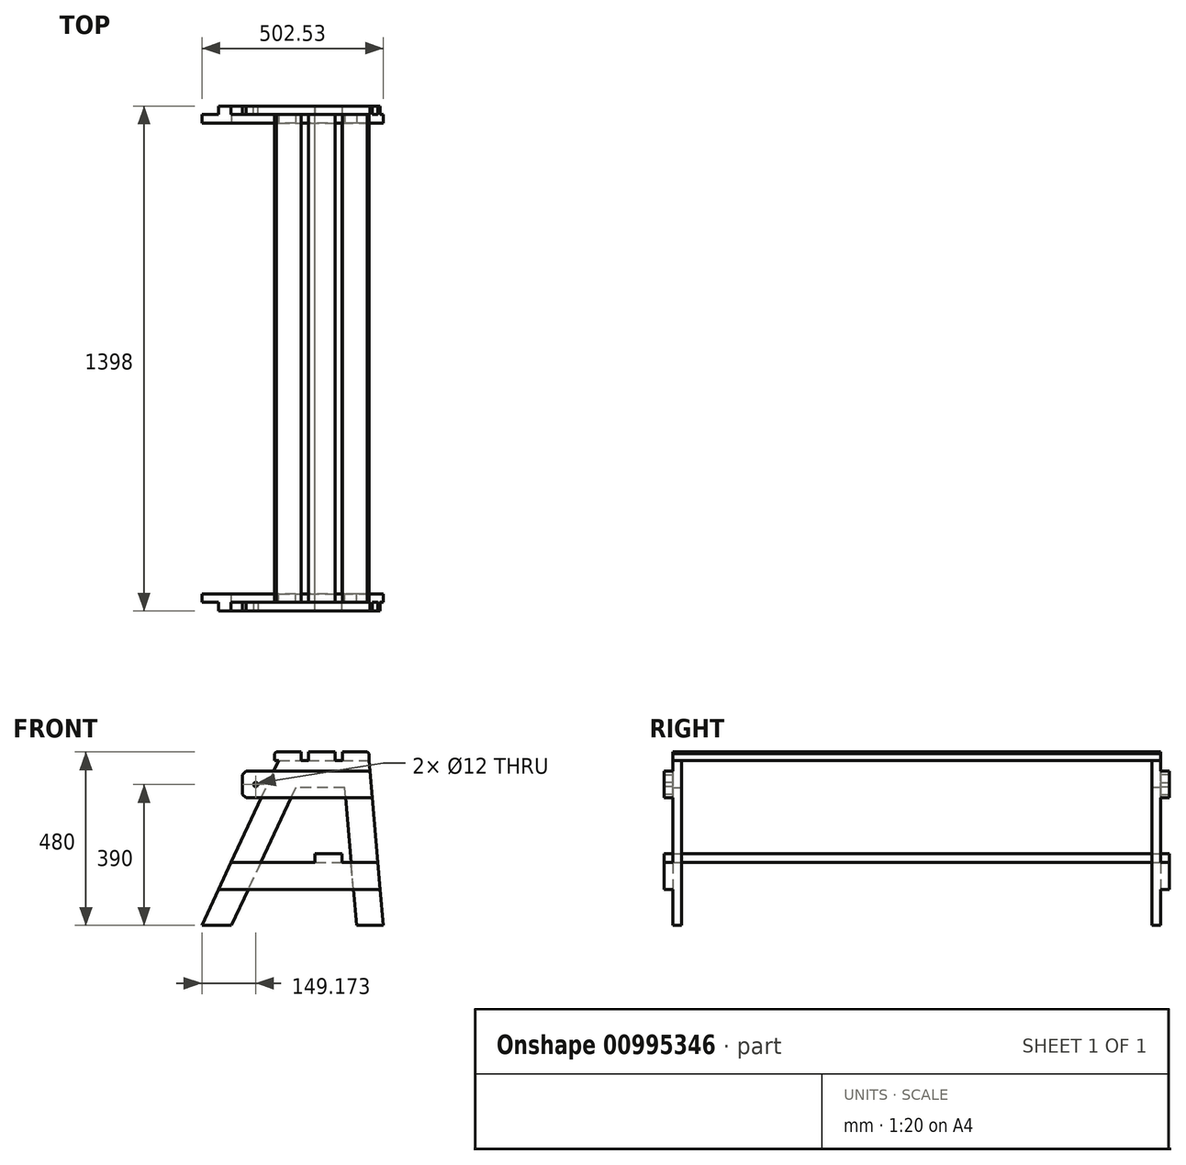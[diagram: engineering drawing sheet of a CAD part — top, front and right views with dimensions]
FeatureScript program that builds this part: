
annotation { "Feature Type Name" : "Feature", "Feature Type Description" : "" }
export const myFeature = defineFeature(function(context is Context, id is Id, definition is map)
    precondition{}
    {
        {
            assignVariable(context, id + "F0", {"name" : "Lattendicke", "anyValue" : 24});
        }
        {
            var Q0;
            Q0=qCreatedBy(makeId("Front.planeOp"),FACE);
            var sketch = newSketch(context, id + "F1", { "sketchPlane" : qUnion([Q0])});
            skLineSegment(sketch, "E0", {"start": v(0, 0) * mm, "end": v(212.64, 456) * mm});
            skLineSegment(sketch, "E1", {"start": v(212.64, 456) * mm, "end": v(462.64, 456) * mm});
            skLineSegment(sketch, "E2", {"start": v(462.64, 456) * mm, "end": v(502.53, 0) * mm});
            skLineSegment(sketch, "E3", {"start": v(502.53, 0) * mm, "end": v(428.25, 0) * mm});
            skLineSegment(sketch, "E4", {"start": v(428.25, 0) * mm, "end": v(394.83, 382) * mm});
            skLineSegment(sketch, "E5", {"start": v(394.83, 382) * mm, "end": v(259.78, 382) * mm});
            skLineSegment(sketch, "E6", {"start": v(259.78, 382) * mm, "end": v(81.65, 0) * mm});
            skLineSegment(sketch, "E7", {"start": v(81.65, 0) * mm, "end": v(0, 0) * mm});
            skSolve(sketch);
        }
        {
            var Q0;
            Q0 = qSketchRegion(id + "F1", true);
            extrude(context, id + "F2", {"entities" : qUnion([Q0]), "depth" : (getVariable(context, 'Lattendicke')) * mm, "offsetDistance" : 25 * mm});
        }
        {
            var Q0;
            Q0=makeQuery(id+"F2.opExtrude","CAP_FACE",FACE,{"disambiguationData":[OSD([sQuery(id+"F1.wireOp",EDGE,"E0"),sQuery(id+"F1.wireOp",EDGE,"E1"),sQuery(id+"F1.wireOp",EDGE,"E2"),sQuery(id+"F1.wireOp",EDGE,"E3"),sQuery(id+"F1.wireOp",EDGE,"E4"),sQuery(id+"F1.wireOp",EDGE,"E5"),sQuery(id+"F1.wireOp",EDGE,"E6"),sQuery(id+"F1.wireOp",EDGE,"E7")])],"isStart":false});
            var sketch = newSketch(context, id + "F3", { "sketchPlane" : qUnion([Q0])});
            skLineSegment(sketch, "E8", {"start": v(465.17, 427) * mm, "end": v(112.17, 427) * mm});
            skLineSegment(sketch, "E9", {"start": v(112.17, 427) * mm, "end": v(112.17, 353) * mm});
            skLineSegment(sketch, "E10", {"start": v(112.17, 353) * mm, "end": v(471.65, 353) * mm});
            skLineSegment(sketch, "E11", {"start": v(471.65, 353) * mm, "end": v(465.17, 427) * mm});
            skLineSegment(sketch, "E12", {"start": v(81.14, 174) * mm, "end": v(487.3, 174) * mm});
            skLineSegment(sketch, "E13", {"start": v(487.3, 174) * mm, "end": v(493.78, 100) * mm});
            skLineSegment(sketch, "E14", {"start": v(493.78, 100) * mm, "end": v(46.63, 100) * mm});
            skLineSegment(sketch, "E15", {"start": v(46.63, 100) * mm, "end": v(81.14, 174) * mm});
            skSolve(sketch);
        }
        {
            var Q0;
            {var subQ3=sQuery(id+"F3.wireOp",EDGE,"E9");Q0=makeQuery(id+"F3.imprint","IMPRINT",FACE,{"disambiguationData":[TD([[makeQuery(id+"F3.imprint","IMPRINT",EDGE,{"derivedFrom":subQ3}),1.0]])]});}
            var Q1;
            {var subQ2=sQuery(id+"F3.wireOp",EDGE,"E11");Q1=makeQuery(id+"F3.imprint","IMPRINT",FACE,{"disambiguationData":[TD([[makeQuery(id+"F3.imprint","IMPRINT",EDGE,{"derivedFrom":subQ2}),-1.0]])]});}
            var Q2;
            {var subQ0=sQuery(id+"F3.wireOp",EDGE,"E12");var subQ1=makeQuery(id+"F2.opExtrude","CAP_EDGE",EDGE,{"disambiguationData":[OSD([sQuery(id+"F1.wireOp",EDGE,"E6")])],"isStart":false});var subQ2=makeQuery(id+"F3.imprint","INTERSECT",VERTEX,{"derivedFrom":[subQ1,subQ0]});Q2=makeQuery(id+"F3.imprint","IMPRINT",FACE,{"disambiguationData":[TD([[makeQuery(id+"F3.imprint","IMPRINT",EDGE,{"disambiguationData":[TD([[subQ2,-1.0]])],"derivedFrom":subQ0}),-1.0]])]});}
            var Q3;
            {var subQ0=sQuery(id+"F3.wireOp",EDGE,"E15");Q3=makeQuery(id+"F3.imprint","IMPRINT",FACE,{"disambiguationData":[TD([[makeQuery(id+"F3.imprint","IMPRINT",EDGE,{"derivedFrom":subQ0}),-1.0]])]});}
            var Q4;
            {var subQ0=sQuery(id+"F3.wireOp",EDGE,"E13");Q4=makeQuery(id+"F3.imprint","IMPRINT",FACE,{"disambiguationData":[TD([[makeQuery(id+"F3.imprint","IMPRINT",EDGE,{"derivedFrom":subQ0}),-1.0]])]});}
            var Q5;
            {var subQ5=makeQuery(id+"F2.opExtrude","CAP_EDGE",EDGE,{"disambiguationData":[OSD([sQuery(id+"F1.wireOp",EDGE,"E5")])],"isStart":false});Q5=makeQuery(id+"F3.imprint","IMPRINT",FACE,{"disambiguationData":[TD([[makeQuery(id+"F3.imprint","IMPRINT",EDGE,{"derivedFrom":subQ5}),1.0]])]});}
            extrude(context, id + "F4", {"entities" : qUnion([Q0, Q1, Q2, Q3, Q4, Q5]), "operationType" : NewBodyOperationType.ADD, "depth" : (getVariable(context, 'Lattendicke')) * mm, "offsetDistance" : 25 * mm});
        }
        {
            var Q0;
            Q0=makeQuery(id+"F4.opExtrude","SWEPT_FACE",FACE,{"disambiguationData":[OSD([sQuery(id+"F3.wireOp",EDGE,"E12")])]});
            var sketch = newSketch(context, id + "F5", { "sketchPlane" : qUnion([Q0])});
            skLineSegment(sketch, "E16.bottom", {"start": v(313.3, -48) * mm, "end": v(387.3, -48) * mm});
            skLineSegment(sketch, "E16.top", {"start": v(313.3, 651) * mm, "end": v(387.3, 651) * mm});
            skLineSegment(sketch, "E16.left", {"start": v(313.3, -48) * mm, "end": v(313.3, 651) * mm});
            skLineSegment(sketch, "E16.right", {"start": v(387.3, -48) * mm, "end": v(387.3, 651) * mm});
            skLineSegment(sketch, "E17", {"start": v(350.3, -48) * mm, "end": v(350.3, 651) * mm, "construction": true});
            skSolve(sketch);
        }
        {
            var Q0;
            Q0 = qSketchRegion(id + "F5", true);
            extrude(context, id + "F6", {"entities" : qUnion([Q0]), "operationType" : NewBodyOperationType.ADD, "depth" : (getVariable(context, 'Lattendicke')) * mm, "offsetDistance" : 25 * mm});
        }
        {
            var Q0;
            Q0=makeQuery(id+"FZW4tMHVHPS0k4L_1.boolean.opBoolean","MERGE",FACE,{"derivedFrom":[makeQuery(id+"F4.opExtrude","CAP_FACE",FACE,{"disambiguationData":[OSD([sQuery(id+"F3.wireOp",EDGE,"E8"),sQuery(id+"F3.wireOp",EDGE,"E9"),sQuery(id+"F3.wireOp",EDGE,"E10"),sQuery(id+"F3.wireOp",EDGE,"E11")])],"isStart":false}),makeQuery(id+"FZW4tMHVHPS0k4L_1.opExtrude","SWEPT_FACE",FACE,{"disambiguationData":[OSD([sQuery(id+"FmopSP1TCN60EbX_1.wireOp",EDGE,"fZKEBfGV-dzuW-k69T-f120-0Okk8d1ObTub.bottom")])]}),makeQuery(id+"FZW4tMHVHPS0k4L_1.opExtrude","SWEPT_FACE",FACE,{"disambiguationData":[OSD([sQuery(id+"FmopSP1TCN60EbX_1.wireOp",EDGE,"MPfSMtai-v8oZ-TTrc-7ozS-PhWWdRkUMMTi.bottom")])]}),makeQuery(id+"FZW4tMHVHPS0k4L_1.opExtrude","SWEPT_FACE",FACE,{"disambiguationData":[OSD([sQuery(id+"FmopSP1TCN60EbX_1.wireOp",EDGE,"9iwYwjk1-Ofcv-kupA-KBHU-Erxazx1jPGkJ.bottom")])]})]});
            var sketch = newSketch(context, id + "F7", { "sketchPlane" : qUnion([Q0])});
            skCircle(sketch, "E18", {"center": v(149.17, 390) * mm, "radius": 6 * mm});
            skSolve(sketch);
        }
        {
            var Q0;
            Q0=makeQuery(id+"F7.imprint","IMPRINT",FACE,{"disambiguationData":[TD([[makeQuery(id+"F7.imprint","IMPRINT",EDGE,{"derivedFrom":sQuery(id+"F7.wireOp",EDGE,"E18")}),1.0]])]});
            extrude(context, id + "F8", {"entities" : qUnion([Q0]), "operationType" : NewBodyOperationType.REMOVE, "endBound" : BoundingType.THROUGH_ALL, "oppositeDirection" : true, "depth" : 25 * mm, "offsetDistance" : 25 * mm});
        }
        {
            var Q0;
            Q0=makeQuery(id+"F4.opExtrude","SWEPT_EDGE",EDGE,{"disambiguationData":[OSD([sQuery(id+"F3.wireOp",EDGE,"E8"),sQuery(id+"F3.wireOp",EDGE,"E9")])]});
            var Q1;
            Q1=makeQuery(id+"F4.opExtrude","SWEPT_EDGE",EDGE,{"disambiguationData":[OSD([sQuery(id+"F3.wireOp",EDGE,"E9"),sQuery(id+"F3.wireOp",EDGE,"E10")])]});
            chamfer(context, id + "F9", {"entities" : qUnion([Q0, Q1]), "width" : 10 * mm, "tangentPropagation" : true});
        }
        {
            var Q0;
            Q0=makeQuery(id+"F2.opExtrude","SWEPT_FACE",FACE,{"disambiguationData":[OSD([sQuery(id+"F1.wireOp",EDGE,"E1")])]});
            var sketch = newSketch(context, id + "F10", { "sketchPlane" : qUnion([Q0])});
            skLineSegment(sketch, "E19.bottom", {"start": v(462.64, -24) * mm, "end": v(388.64, -24) * mm});
            skLineSegment(sketch, "E19.top", {"start": v(462.64, 651) * mm, "end": v(388.64, 651) * mm});
            skLineSegment(sketch, "E19.left", {"start": v(462.64, -24) * mm, "end": v(462.64, 651) * mm});
            skLineSegment(sketch, "E19.right", {"start": v(388.64, -24) * mm, "end": v(388.64, 651) * mm});
            skLineSegment(sketch, "E20.bottom", {"start": v(368.64, -24) * mm, "end": v(294.64, -24) * mm});
            skLineSegment(sketch, "E20.top", {"start": v(368.64, 651) * mm, "end": v(294.64, 651) * mm});
            skLineSegment(sketch, "E20.left", {"start": v(368.64, -24) * mm, "end": v(368.64, 651) * mm});
            skLineSegment(sketch, "E20.right", {"start": v(294.64, -24) * mm, "end": v(294.64, 651) * mm});
            skLineSegment(sketch, "E21.bottom", {"start": v(274.64, -24) * mm, "end": v(200.64, -24) * mm});
            skLineSegment(sketch, "E21.top", {"start": v(274.64, 651) * mm, "end": v(200.64, 651) * mm});
            skLineSegment(sketch, "E21.left", {"start": v(274.64, -24) * mm, "end": v(274.64, 651) * mm});
            skLineSegment(sketch, "E21.right", {"start": v(200.64, -24) * mm, "end": v(200.64, 651) * mm});
            skSolve(sketch);
        }
        {
            var Q0;
            {var subQ0=sQuery(id+"F10.wireOp",EDGE,"E19.top");Q0=makeQuery(id+"F10.imprint","IMPRINT",FACE,{"disambiguationData":[TD([[makeQuery(id+"F10.imprint","IMPRINT",EDGE,{"derivedFrom":subQ0}),1.0]])]});}
            var Q1;
            {var subQ0=sQuery(id+"F10.wireOp",EDGE,"E20.top");Q1=makeQuery(id+"F10.imprint","IMPRINT",FACE,{"disambiguationData":[TD([[makeQuery(id+"F10.imprint","IMPRINT",EDGE,{"derivedFrom":subQ0}),1.0]])]});}
            var Q2;
            {var subQ0=sQuery(id+"F10.wireOp",EDGE,"E19.bottom");Q2=makeQuery(id+"F10.imprint","IMPRINT",FACE,{"disambiguationData":[TD([[makeQuery(id+"F10.imprint","IMPRINT",EDGE,{"derivedFrom":subQ0}),1.0]])]});}
            var Q3;
            {var subQ0=sQuery(id+"F10.wireOp",EDGE,"E20.bottom");Q3=makeQuery(id+"F10.imprint","IMPRINT",FACE,{"disambiguationData":[TD([[makeQuery(id+"F10.imprint","IMPRINT",EDGE,{"derivedFrom":subQ0}),1.0]])]});}
            var Q4;
            {var subQ0=sQuery(id+"F10.wireOp",EDGE,"E21.bottom");Q4=makeQuery(id+"F10.imprint","IMPRINT",FACE,{"disambiguationData":[TD([[makeQuery(id+"F10.imprint","IMPRINT",EDGE,{"derivedFrom":subQ0}),1.0]])]});}
            var Q5;
            {var subQ0=sQuery(id+"F10.wireOp",EDGE,"E21.top");Q5=makeQuery(id+"F10.imprint","IMPRINT",FACE,{"disambiguationData":[TD([[makeQuery(id+"F10.imprint","IMPRINT",EDGE,{"derivedFrom":subQ0}),1.0]])]});}
            extrude(context, id + "F11", {"entities" : qUnion([Q0, Q1, Q2, Q3, Q4, Q5]), "operationType" : NewBodyOperationType.ADD, "depth" : (getVariable(context, 'Lattendicke')) * mm, "offsetDistance" : 25 * mm});
        }
        {
            var Q0;
            Q0=makeQuery(id+"F11.opExtrude","CAP_EDGE",EDGE,{"disambiguationData":[OSD([sQuery(id+"F10.wireOp",EDGE,"E21.right")])],"isStart":false});
            var Q1;
            Q1=makeQuery(id+"F11.opExtrude","CAP_EDGE",EDGE,{"disambiguationData":[OSD([sQuery(id+"F10.wireOp",EDGE,"E19.left")])],"isStart":false});
            chamfer(context, id + "F12", {"entities" : qUnion([Q0, Q1]), "width" : 5 * mm, "tangentPropagation" : true});
        }
        {
            var Q0;
            Q0=makeQuery(id+"F2.opExtrude","SWEPT_BODY",BODY,{"disambiguationData":[OSD([sQuery(id+"F1.wireOp",EDGE,"E0"),sQuery(id+"F1.wireOp",EDGE,"E1"),sQuery(id+"F1.wireOp",EDGE,"E2"),sQuery(id+"F1.wireOp",EDGE,"E3"),sQuery(id+"F1.wireOp",EDGE,"E4"),sQuery(id+"F1.wireOp",EDGE,"E5"),sQuery(id+"F1.wireOp",EDGE,"E6"),sQuery(id+"F1.wireOp",EDGE,"E7")])]});
            var Q1;
            Q1=makeQuery(id+"F6.opExtrude","SWEPT_FACE",FACE,{"disambiguationData":[OSD([sQuery(id+"F5.wireOp",EDGE,"E16.top")])]});
            mirror(context, id + "F13", {"operationType" : NewBodyOperationType.ADD, "entities" : qUnion([Q0]), "mirrorPlane" : qUnion([Q1])});
        }
    });
